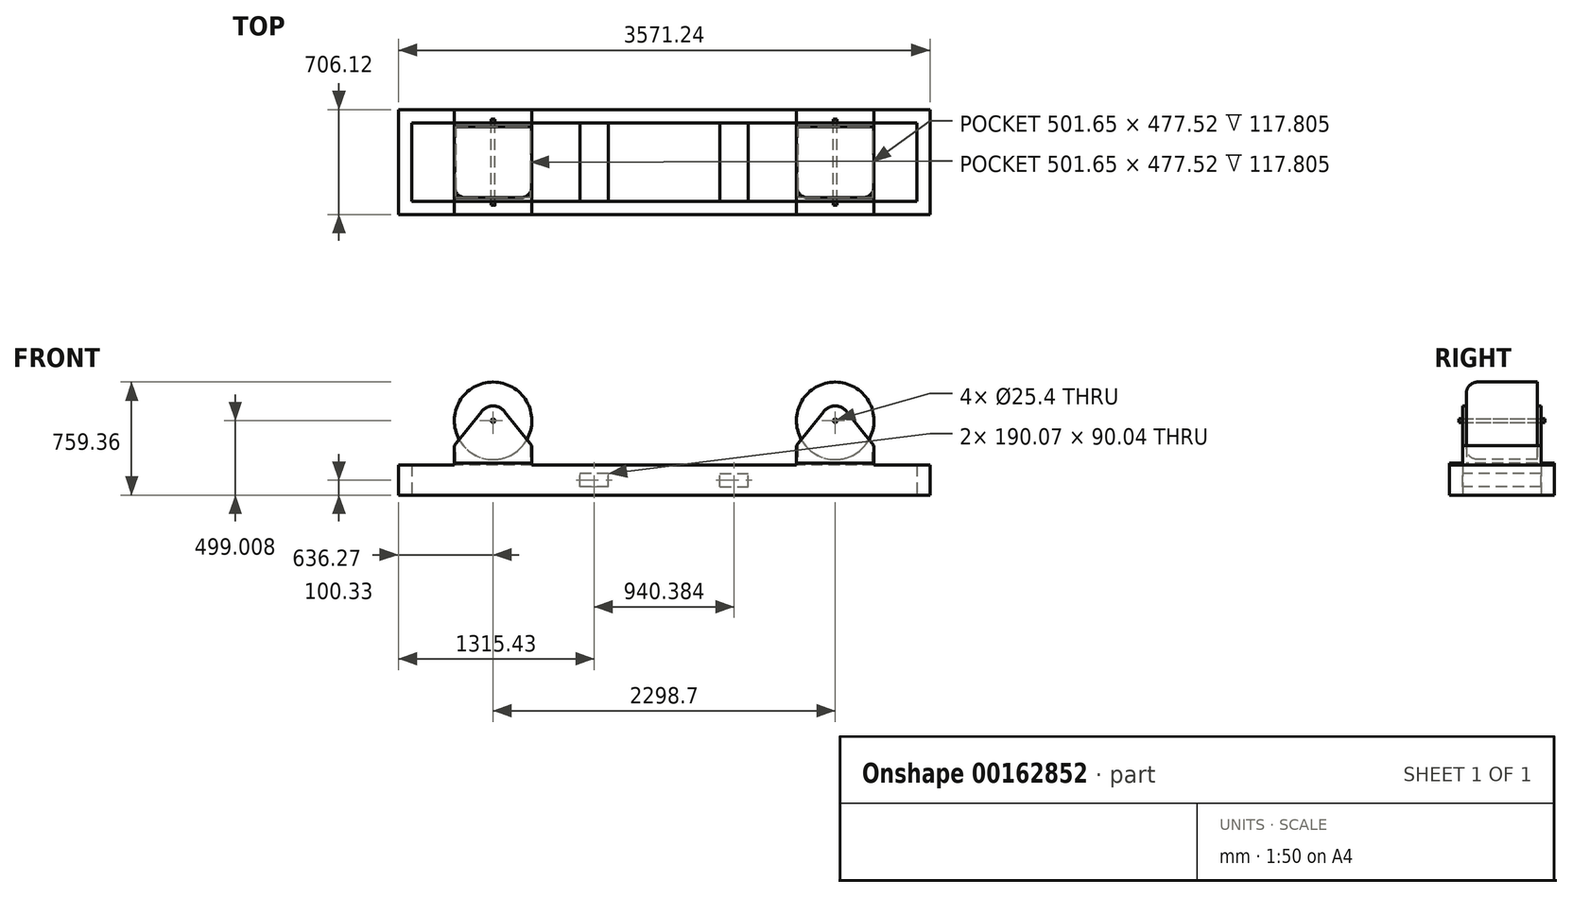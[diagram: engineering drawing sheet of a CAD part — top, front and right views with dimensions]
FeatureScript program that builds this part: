
annotation { "Feature Type Name" : "Feature", "Feature Type Description" : "" }
export const myFeature = defineFeature(function(context is Context, id is Id, definition is map)
    precondition{}
    {
        {
            var Q0;
            Q0=qCreatedBy(makeId("Top.planeOp"),FACE);
            var sketch = newSketch(context, id + "F0", { "sketchPlane" : qUnion([Q0])});
            skLineSegment(sketch, "E0.bottom", {"start": v(1785.62, -353.06) * mm, "end": v(-1785.62, -353.06) * mm});
            skLineSegment(sketch, "E0.top", {"start": v(1785.62, 353.06) * mm, "end": v(-1785.62, 353.06) * mm});
            skLineSegment(sketch, "E0.left", {"start": v(1785.62, -353.06) * mm, "end": v(1785.62, 353.06) * mm});
            skLineSegment(sketch, "E0.right", {"start": v(-1785.62, -353.06) * mm, "end": v(-1785.62, 353.06) * mm});
            skPoint(sketch, "E0.middle", {"position": v(0, 0) * mm});
            skLineSegment(sketch, "E1.bottom", {"start": v(1696.72, -264.16) * mm, "end": v(-1696.72, -264.16) * mm});
            skLineSegment(sketch, "E1.top", {"start": v(1696.72, 264.16) * mm, "end": v(-1696.72, 264.16) * mm});
            skLineSegment(sketch, "E1.left", {"start": v(1696.72, -264.16) * mm, "end": v(1696.72, 264.16) * mm});
            skLineSegment(sketch, "E1.right", {"start": v(-1696.72, -264.16) * mm, "end": v(-1696.72, 264.16) * mm});
            skSolve(sketch);
        }
        {
            var Q0;
            Q0 = qSketchRegion(id + "F0", true);
            extrude(context, id + "F1", {"entities" : qUnion([Q0]), "depth" : 200.66 * mm});
        }
        {
            var Q0;
            Q0=makeQuery(id+"F1.opExtrude","SWEPT_FACE",FACE,{"disambiguationData":[OSD([sQuery(id+"F0.wireOp",EDGE,"E0.bottom")])]});
            var sketch = newSketch(context, id + "F2", { "sketchPlane" : qUnion([Q0])});
            skLineSegment(sketch, "E2", {"start": v(0, 0) * mm, "end": v(0, 200.66) * mm});
            skLineSegment(sketch, "E3.bottom", {"start": v(-375.16, 55.3) * mm, "end": v(-565.23, 55.3) * mm});
            skLineSegment(sketch, "E3.top", {"start": v(-375.16, 145.35) * mm, "end": v(-565.23, 145.35) * mm});
            skLineSegment(sketch, "E3.left", {"start": v(-375.16, 55.3) * mm, "end": v(-375.16, 145.35) * mm});
            skLineSegment(sketch, "E3.right", {"start": v(-565.23, 55.3) * mm, "end": v(-565.23, 145.35) * mm});
            skPoint(sketch, "E3.middle", {"position": v(-470.2, 100.33) * mm});
            skPoint(sketch, "E3.middle.positionSnap0", {"position": v(0, 100.33) * mm});
            skPoint(sketch, "E3.centerSnap0", {"position": v(0, 100.33) * mm});
            skLineSegment(sketch, "E4.MirrorCS", {"start": v(375.16, 145.35) * mm, "end": v(565.23, 145.35) * mm});
            skLineSegment(sketch, "E5.MirrorCS", {"start": v(375.16, 55.3) * mm, "end": v(375.16, 145.35) * mm});
            skLineSegment(sketch, "E6.MirrorCS", {"start": v(375.16, 55.3) * mm, "end": v(565.23, 55.3) * mm});
            skLineSegment(sketch, "E7.MirrorCS", {"start": v(565.23, 55.3) * mm, "end": v(565.23, 145.35) * mm});
            skSolve(sketch);
        }
        {
            var Q0;
            Q0 = qSketchRegion(id + "F2", true);
            var Q1;
            Q1=makeQuery(id+"F1.opExtrude","SWEPT_FACE",FACE,{"disambiguationData":[OSD([sQuery(id+"F0.wireOp",EDGE,"E0.top")])]});
            extrude(context, id + "F3", {"entities" : qUnion([Q0]), "operationType" : NewBodyOperationType.ADD, "endBound" : BoundingType.UP_TO_SURFACE, "oppositeDirection" : true, "endBoundEntityFace" : qUnion([Q1]), "depth" : 25.4 * mm});
        }
        {
            var Q0;
            Q0=makeQuery(id+"F1.opExtrude","CAP_FACE",FACE,{"disambiguationData":[OSD([sQuery(id+"F0.wireOp",EDGE,"E0.bottom"),sQuery(id+"F0.wireOp",EDGE,"E0.top"),sQuery(id+"F0.wireOp",EDGE,"E0.left"),sQuery(id+"F0.wireOp",EDGE,"E0.right"),sQuery(id+"F0.wireOp",EDGE,"E1.bottom"),sQuery(id+"F0.wireOp",EDGE,"E1.top"),sQuery(id+"F0.wireOp",EDGE,"E1.left"),sQuery(id+"F0.wireOp",EDGE,"E1.right")])],"isStart":false});
            var sketch = newSketch(context, id + "F4", { "sketchPlane" : qUnion([Q0])});
            skLineSegment(sketch, "E8.bottom", {"start": v(-1409.7, 353.06) * mm, "end": v(-889, 353.06) * mm});
            skLineSegment(sketch, "E8.top", {"start": v(-1409.7, -353.06) * mm, "end": v(-889, -353.06) * mm});
            skLineSegment(sketch, "E8.left", {"start": v(-1409.7, 353.06) * mm, "end": v(-1409.7, -353.06) * mm});
            skLineSegment(sketch, "E8.right", {"start": v(-889, 353.06) * mm, "end": v(-889, -353.06) * mm});
            skLineSegment(sketch, "E9.MirrorCS", {"start": v(1409.7, 353.06) * mm, "end": v(889, 353.06) * mm});
            skLineSegment(sketch, "E10.MirrorCS", {"start": v(889, 353.06) * mm, "end": v(889, -353.06) * mm});
            skLineSegment(sketch, "E11.MirrorCS", {"start": v(1409.7, 353.06) * mm, "end": v(1409.7, -353.06) * mm});
            skLineSegment(sketch, "E12.MirrorCS", {"start": v(1409.7, -353.06) * mm, "end": v(889, -353.06) * mm});
            skSolve(sketch);
        }
        {
            var Q0;
            Q0 = qSketchRegion(id + "F4", true);
            extrude(context, id + "F5", {"entities" : qUnion([Q0]), "operationType" : NewBodyOperationType.ADD, "depth" : 12.7 * mm});
        }
        {
            var Q0;
            Q0=makeQuery(id+"F5.opExtrude","CAP_FACE",FACE,{"disambiguationData":[OSD([sQuery(id+"F4.wireOp",EDGE,"E8.bottom"),sQuery(id+"F4.wireOp",EDGE,"E8.top"),sQuery(id+"F4.wireOp",EDGE,"E8.left"),sQuery(id+"F4.wireOp",EDGE,"E8.right")])],"isStart":false});
            var sketch = newSketch(context, id + "F6", { "sketchPlane" : qUnion([Q0])});
            skLineSegment(sketch, "E13.bottom", {"start": v(-1409.7, 264.16) * mm, "end": v(-889, 264.16) * mm});
            skLineSegment(sketch, "E13.top", {"start": v(-1409.7, 238.76) * mm, "end": v(-889, 238.76) * mm});
            skLineSegment(sketch, "E13.left", {"start": v(-1409.7, 264.16) * mm, "end": v(-1409.7, 238.76) * mm});
            skLineSegment(sketch, "E13.right", {"start": v(-889, 264.16) * mm, "end": v(-889, 238.76) * mm});
            skLineSegment(sketch, "E14.MirrorCS", {"start": v(1409.7, 264.16) * mm, "end": v(889, 264.16) * mm});
            skLineSegment(sketch, "E15.MirrorCS", {"start": v(1409.7, 238.76) * mm, "end": v(889, 238.76) * mm});
            skLineSegment(sketch, "E16.MirrorCS", {"start": v(1409.7, 264.16) * mm, "end": v(1409.7, 238.76) * mm});
            skLineSegment(sketch, "E17.MirrorCS", {"start": v(889, 264.16) * mm, "end": v(889, 238.76) * mm});
            skLineSegment(sketch, "E18.MirrorCS", {"start": v(889, -264.16) * mm, "end": v(889, -238.76) * mm});
            skLineSegment(sketch, "E19.MirrorCS", {"start": v(1409.7, -264.16) * mm, "end": v(1409.7, -238.76) * mm});
            skLineSegment(sketch, "E20.MirrorCS", {"start": v(-889, -264.16) * mm, "end": v(-889, -238.76) * mm});
            skLineSegment(sketch, "E21.MirrorCS", {"start": v(-1409.7, -264.16) * mm, "end": v(-1409.7, -238.76) * mm});
            skLineSegment(sketch, "E22.MirrorCS", {"start": v(1409.7, -238.76) * mm, "end": v(889, -238.76) * mm});
            skLineSegment(sketch, "E23.MirrorCS", {"start": v(1409.7, -264.16) * mm, "end": v(889, -264.16) * mm});
            skLineSegment(sketch, "E24.MirrorCS", {"start": v(-1409.7, -238.76) * mm, "end": v(-889, -238.76) * mm});
            skLineSegment(sketch, "E25.MirrorCS", {"start": v(-1409.7, -264.16) * mm, "end": v(-889, -264.16) * mm});
            skSolve(sketch);
        }
        {
            var Q0;
            Q0 = qSketchRegion(id + "F6", true);
            extrude(context, id + "F7", {"entities" : qUnion([Q0]), "operationType" : NewBodyOperationType.ADD, "depth" : 385.17 * mm});
        }
        {
            var Q0;
            Q0=makeQuery(id+"F7.opExtrude","SWEPT_FACE",FACE,{"disambiguationData":[OSD([sQuery(id+"F6.wireOp",EDGE,"E25.MirrorCS")])]});
            var sketch = newSketch(context, id + "F8", { "sketchPlane" : qUnion([Q0])});
            skArc(sketch, "E26", {"start": v(-1072.14, 561.3) * mm, "mid": v(-1149.35, 598.53) * mm, "end": v(-1226.56, 561.3) * mm});
            skLineSegment(sketch, "E27", {"start": v(-1409.7, 331.17) * mm, "end": v(-1226.56, 561.3) * mm});
            skLineSegment(sketch, "E28", {"start": v(-889, 331.17) * mm, "end": v(-1072.14, 561.3) * mm});
            skPoint(sketch, "E29.orphan", {"position": v(-1149.35, 598.53) * mm});
            skLineSegment(sketch, "E30", {"start": v(-1409.7, 331.17) * mm, "end": v(-1409.7, 598.53) * mm});
            skLineSegment(sketch, "E31", {"start": v(-1409.7, 598.53) * mm, "end": v(-889, 598.53) * mm});
            skLineSegment(sketch, "E32", {"start": v(-889, 598.53) * mm, "end": v(-889, 331.17) * mm});
            skLineSegment(sketch, "E33.MirrorCS", {"start": v(889, 598.53) * mm, "end": v(889, 331.17) * mm});
            skLineSegment(sketch, "E34.MirrorCS", {"start": v(1409.7, 331.17) * mm, "end": v(1226.56, 561.3) * mm});
            skPoint(sketch, "E35.MirrorP", {"position": v(1149.35, 598.53) * mm});
            skLineSegment(sketch, "E36.MirrorCS", {"start": v(1409.7, 331.17) * mm, "end": v(1409.7, 598.53) * mm});
            skLineSegment(sketch, "E37.MirrorCS", {"start": v(1409.7, 598.53) * mm, "end": v(889, 598.53) * mm});
            skArc(sketch, "E38.MirrorCS", {"start": v(1072.14, 561.3) * mm, "mid": v(1149.35, 598.53) * mm, "end": v(1226.56, 561.3) * mm});
            skLineSegment(sketch, "E39.MirrorCS", {"start": v(889, 331.17) * mm, "end": v(1072.14, 561.3) * mm});
            skSolve(sketch);
        }
        {
            var Q0;
            Q0 = qSketchRegion(id + "F8", true);
            extrude(context, id + "F9", {"entities" : qUnion([Q0]), "operationType" : NewBodyOperationType.REMOVE, "endBound" : BoundingType.THROUGH_ALL, "oppositeDirection" : true, "depth" : 25.4 * mm});
        }
        {
            var Q0;
            Q0=makeQuery(id+"F7.opExtrude","SWEPT_FACE",FACE,{"disambiguationData":[OSD([sQuery(id+"F6.wireOp",EDGE,"E24.MirrorCS")])]});
            var sketch = newSketch(context, id + "F10", { "sketchPlane" : qUnion([Q0])});
            skLineSegment(sketch, "E40.bottom", {"start": v(1409.7, 331.17) * mm, "end": v(1400.18, 331.17) * mm});
            skLineSegment(sketch, "E40.top", {"start": v(1409.7, 213.36) * mm, "end": v(1400.18, 213.36) * mm});
            skLineSegment(sketch, "E40.left", {"start": v(1409.7, 331.17) * mm, "end": v(1409.7, 213.36) * mm});
            skLineSegment(sketch, "E40.right", {"start": v(1400.18, 331.17) * mm, "end": v(1400.18, 213.36) * mm});
            skLineSegment(sketch, "E41.MirrorCS", {"start": v(-1409.7, 331.17) * mm, "end": v(-1400.18, 331.17) * mm});
            skLineSegment(sketch, "E42.MirrorCS", {"start": v(-1409.7, 213.36) * mm, "end": v(-1400.18, 213.36) * mm});
            skLineSegment(sketch, "E43.MirrorCS", {"start": v(-1409.7, 331.17) * mm, "end": v(-1409.7, 213.36) * mm});
            skLineSegment(sketch, "E44.MirrorCS", {"start": v(-1400.18, 331.17) * mm, "end": v(-1400.18, 213.36) * mm});
            skSolve(sketch);
        }
        {
            var Q0;
            Q0 = qSketchRegion(id + "F10", true);
            var Q1;
            Q1=makeQuery(id+"F7.opExtrude","SWEPT_FACE",FACE,{"disambiguationData":[OSD([sQuery(id+"F6.wireOp",EDGE,"E15.MirrorCS")])]});
            extrude(context, id + "F11", {"entities" : qUnion([Q0]), "operationType" : NewBodyOperationType.ADD, "endBound" : BoundingType.UP_TO_SURFACE, "endBoundEntityFace" : qUnion([Q1]), "depth" : 25.4 * mm});
        }
        {
            var Q0;
            Q0=makeQuery(id+"F7.opExtrude","SWEPT_FACE",FACE,{"disambiguationData":[OSD([sQuery(id+"F6.wireOp",EDGE,"E24.MirrorCS")])]});
            var sketch = newSketch(context, id + "F12", { "sketchPlane" : qUnion([Q0])});
            skLineSegment(sketch, "E45.bottom", {"start": v(889, 331.17) * mm, "end": v(898.52, 331.17) * mm});
            skLineSegment(sketch, "E45.top", {"start": v(889, 213.36) * mm, "end": v(898.52, 213.36) * mm});
            skLineSegment(sketch, "E45.left", {"start": v(889, 331.17) * mm, "end": v(889, 213.36) * mm});
            skLineSegment(sketch, "E45.right", {"start": v(898.52, 331.17) * mm, "end": v(898.52, 213.36) * mm});
            skLineSegment(sketch, "E46.MirrorCS", {"start": v(-889, 213.36) * mm, "end": v(-898.52, 213.36) * mm});
            skLineSegment(sketch, "E47.MirrorCS", {"start": v(-889, 331.17) * mm, "end": v(-898.52, 331.17) * mm});
            skLineSegment(sketch, "E48.MirrorCS", {"start": v(-898.52, 331.17) * mm, "end": v(-898.52, 213.36) * mm});
            skLineSegment(sketch, "E49.MirrorCS", {"start": v(-889, 331.17) * mm, "end": v(-889, 213.36) * mm});
            skSolve(sketch);
        }
        {
            var Q0;
            Q0 = qSketchRegion(id + "F12", true);
            var Q1;
            Q1=makeQuery(id+"F7.opExtrude","SWEPT_FACE",FACE,{"disambiguationData":[OSD([sQuery(id+"F6.wireOp",EDGE,"E13.top")])]});
            extrude(context, id + "F13", {"entities" : qUnion([Q0]), "operationType" : NewBodyOperationType.ADD, "endBound" : BoundingType.UP_TO_SURFACE, "endBoundEntityFace" : qUnion([Q1]), "depth" : 25.4 * mm});
        }
        {
            var Q0;
            Q0=makeQuery(id+"F7.opExtrude","SWEPT_FACE",FACE,{"disambiguationData":[OSD([sQuery(id+"F6.wireOp",EDGE,"E14.MirrorCS")])]});
            var sketch = newSketch(context, id + "F14", { "sketchPlane" : qUnion([Q0])});
            skCircle(sketch, "E50", {"center": v(-1149.35, 499) * mm, "radius": 12.7 * mm});
            skPoint(sketch, "E50.centerSnap0", {"position": v(-1149.35, 598.53) * mm});
            skCircle(sketch, "E51.MirrorC", {"center": v(1149.35, 499) * mm, "radius": 12.7 * mm});
            skSolve(sketch);
        }
        {
            var Q0;
            Q0 = qSketchRegion(id + "F14", true);
            extrude(context, id + "F15", {"entities" : qUnion([Q0]), "operationType" : NewBodyOperationType.REMOVE, "endBound" : BoundingType.THROUGH_ALL, "oppositeDirection" : true, "depth" : 25.4 * mm});
        }
        {
            var Q0;
            Q0=makeQuery(id+"F7.opExtrude","SWEPT_FACE",FACE,{"disambiguationData":[OSD([sQuery(id+"F6.wireOp",EDGE,"E25.MirrorCS")])]});
            var sketch = newSketch(context, id + "F16", { "sketchPlane" : qUnion([Q0])});
            skCircle(sketch, "E52", {"center": v(-1149.35, 499) * mm, "radius": 12.7 * mm});
            skCircle(sketch, "E53.MirrorC", {"center": v(1149.35, 499) * mm, "radius": 12.7 * mm});
            skSolve(sketch);
        }
        {
            var Q0;
            Q0 = qSketchRegion(id + "F16", true);
            extrude(context, id + "F17", {"entities" : qUnion([Q0]), "depth" : 25.4 * mm, "hasSecondDirection" : true, "secondDirectionOppositeDirection" : true, "secondDirectionDepth" : 552.45 * mm});
        }
        {
            var Q0;
            Q0=makeQuery(id+"F7.opExtrude","SWEPT_FACE",FACE,{"disambiguationData":[OSD([sQuery(id+"F6.wireOp",EDGE,"E22.MirrorCS")])]});
            var sketch = newSketch(context, id + "F18", { "sketchPlane" : qUnion([Q0])});
            skCircle(sketch, "E54", {"center": v(-1149.35, 499) * mm, "radius": 260.35 * mm});
            skCircle(sketch, "E55.MirrorC", {"center": v(1149.35, 499) * mm, "radius": 260.35 * mm});
            skSolve(sketch);
        }
        {
            var Q0;
            Q0 = qSketchRegion(id + "F18", true);
            var Q1;
            Q1=makeQuery(id+"F7.opExtrude","SWEPT_FACE",FACE,{"disambiguationData":[OSD([sQuery(id+"F6.wireOp",EDGE,"E15.MirrorCS")])]});
            extrude(context, id + "F19", {"entities" : qUnion([Q0]), "endBound" : BoundingType.UP_TO_SURFACE, "endBoundEntityFace" : qUnion([Q1]), "depth" : 25.4 * mm});
        }
        {
            var Q0;
            {var subQ0=sQuery(id+"F18.wireOp",EDGE,"E54");var subQ1=makeQuery(id+"F7.opExtrude","SWEPT_FACE",FACE,{"disambiguationData":[OSD([sQuery(id+"F6.wireOp",EDGE,"E22.MirrorCS")])]});var subQ2=makeQuery(id+"F18.imprint","INTERSECT",VERTEX,{"derivedFrom":[makeQuery(id+"F9.boolean.opBoolean","INTERSECT",EDGE,{"derivedFrom":[subQ1,makeQuery(id+"F9.opExtrude","SWEPT_FACE",FACE,{"disambiguationData":[OSD([sQuery(id+"F8.wireOp",EDGE,"E39.MirrorCS")])]})]}),subQ0]});Q0=makeQuery(id+"F19.opExtrude","TWEAK_EDGE",EDGE,{"derivedFrom":[makeQuery(id+"F7.opExtrude","SWEPT_FACE",FACE,{"disambiguationData":[OSD([sQuery(id+"F6.wireOp",EDGE,"E15.MirrorCS")])]}),makeQuery(id+"F18.imprint","IMPRINT",EDGE,{"disambiguationData":[TD([[subQ2,1.0]])],"derivedFrom":subQ0}),makeQuery(id+"F18.imprint","IMPRINT",EDGE,{"disambiguationData":[TD([[subQ2,-1.0]])],"derivedFrom":subQ0})]});}
            var Q1;
            Q1=makeQuery(id+"F19.opExtrude","TWEAK_EDGE",EDGE,{"derivedFrom":[makeQuery(id+"F7.opExtrude","SWEPT_FACE",FACE,{"disambiguationData":[OSD([sQuery(id+"F6.wireOp",EDGE,"E15.MirrorCS")])]}),makeQuery(id+"F18.imprint","IMPRINT",EDGE,{"derivedFrom":sQuery(id+"F18.wireOp",EDGE,"E55.MirrorC")})]});
            var Q2;
            Q2=makeQuery(id+"F19.opExtrude","CAP_EDGE",EDGE,{"disambiguationData":[OSD([sQuery(id+"F18.wireOp",EDGE,"E55.MirrorC")])],"isStart":true});
            var Q3;
            Q3=makeQuery(id+"F19.opExtrude","CAP_EDGE",EDGE,{"disambiguationData":[OSD([sQuery(id+"F18.wireOp",EDGE,"E54")])],"isStart":true});
            fillet(context, id + "F20", {"entities" : qUnion([Q0, Q1, Q2, Q3]), "radius" : 76.2 * mm, "tangentPropagation" : true, "allowEdgeOverflow" : false});
        }
    });
